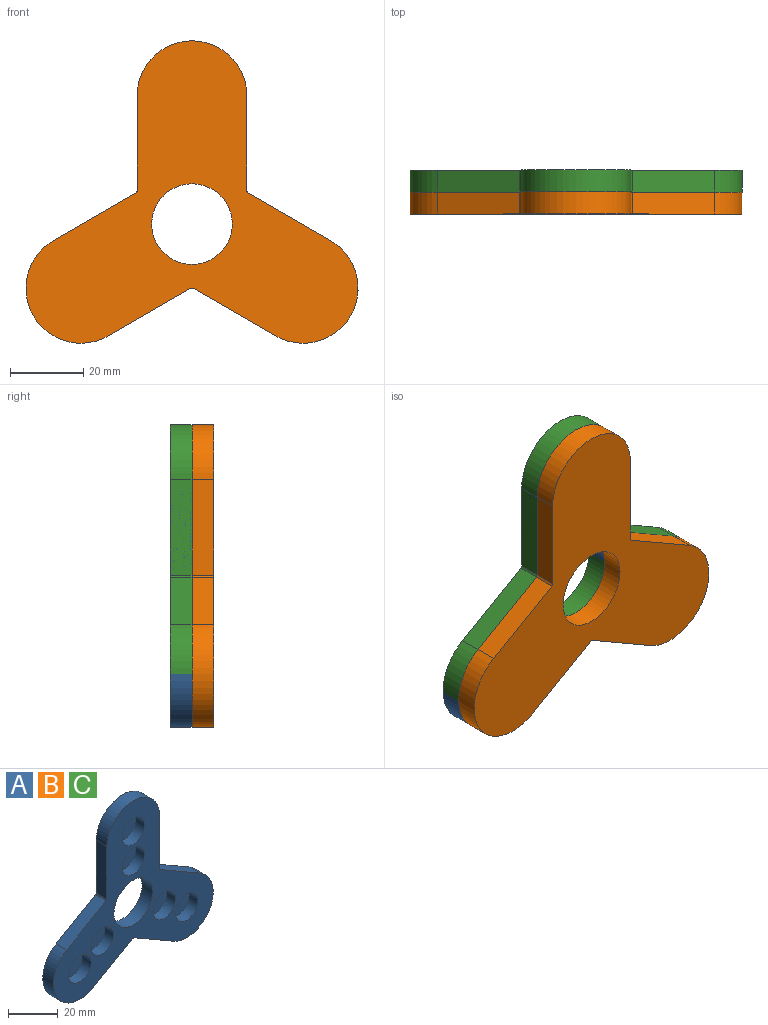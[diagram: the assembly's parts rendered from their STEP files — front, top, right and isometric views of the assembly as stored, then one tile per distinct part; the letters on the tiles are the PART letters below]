
ASSEMBLY  parts=3 mates=1
PART A: 27 faces, bbox 90.6x6x82.5 mm
  f0: plane 22.52x13mm, normal (0.5,0,0.87), area 156mm2, adj f1,f18,f19,f20
  f1: cylinder r=17.5mm len=6mm, axis (0,1,0), area 3.7mm2, adj f0,f2,f19,f20
  f2: plane 26x6mm, normal (1,0,0), area 156mm2, adj f1,f3,f19,f20
  f3: cylinder r=15mm len=30mm, axis (0,1,0), area 282.7mm2, adj f2,f4,f19,f20
  f4: plane 26x6mm, normal (-1,0,0), area 156mm2, adj f3,f5,f19,f20
  f5: cylinder r=17.5mm len=6mm, axis (0,1,0), area 3.7mm2, adj f4,f6,f19,f20
  f6: plane 22.52x13mm, normal (-0.5,0,0.87), area 156mm2, adj f5,f7,f19,f20
  f7: cylinder r=15mm len=27.99mm, axis (0,1,0), area 282.7mm2, adj f6,f8,f19,f20
  f8: plane 22.52x13mm, normal (0.5,0,-0.87), area 156mm2, adj f7,f9,f19,f20
  f9: cylinder r=17.5mm len=6mm, axis (0,1,0), area 3.7mm2, adj f8,f10,f19,f20
  f10: plane 22.52x13mm, normal (-0.5,0,-0.87), area 156mm2, adj f9,f18,f19,f20
  f11: cylinder r=11mm len=22mm, axis (0,1,0), area 414.7mm2, adj f19,f20
  f12: cylinder r=6.35mm len=12.7mm, axis (0,1,0), area 199.5mm2, adj f19,f21
  f13: cylinder r=6.35mm len=12.7mm, axis (0,1,0), area 199.5mm2, adj f19,f22
  f14: cylinder r=6.35mm len=12.7mm, axis (0,1,0), area 199.5mm2, adj f19,f23
  f15: cylinder r=6.35mm len=12.7mm, axis (0,1,0), area 199.5mm2, adj f19,f24
  f16: cylinder r=6.35mm len=12.7mm, axis (0,1,0), area 199.5mm2, adj f19,f25
  f17: cylinder r=6.35mm len=12.7mm, axis (0,1,0), area 199.5mm2, adj f19,f26
  f18: cylinder r=15mm len=27.99mm, axis (0,1,0), area 282.7mm2, adj f0,f10,f19,f20
  f19: plane 90.65x82.52mm, normal (0,-1,0), area 2681.8mm2, adj f0,f1,f2,f3,f4,f5,f6,f7
  f20: plane 90.65x82.52mm, normal (0,1,0), area 3441.9mm2, adj f0,f1,f2,f3,f4,f5,f6,f7
  f21: plane 12.7x12.7mm, normal (0,-1,0), area 126.7mm2, adj f12
  f22: plane 12.7x12.7mm, normal (0,-1,0), area 126.7mm2, adj f13
  f23: plane 12.7x12.7mm, normal (0,-1,0), area 126.7mm2, adj f14
  f24: plane 12.7x12.7mm, normal (0,-1,0), area 126.7mm2, adj f15
  f25: plane 12.7x12.7mm, normal (0,-1,0), area 126.7mm2, adj f16
  f26: plane 12.7x12.7mm, normal (0,-1,0), area 126.7mm2, adj f17
PART B: same geometry as A
PART C: same geometry as A
PLACE A t=(2.66,8.25,-1.68)mm
PLACE B rot(axis=(0,0,1),180deg) t=(2.66,-3.75,-1.68)mm
PLACE C t=(2.66,8.25,-1.68)mm
MATE fastened B.f9 <-> A.f11  axis (0,1,0) through (2.66,2.25,-1.68)mm
